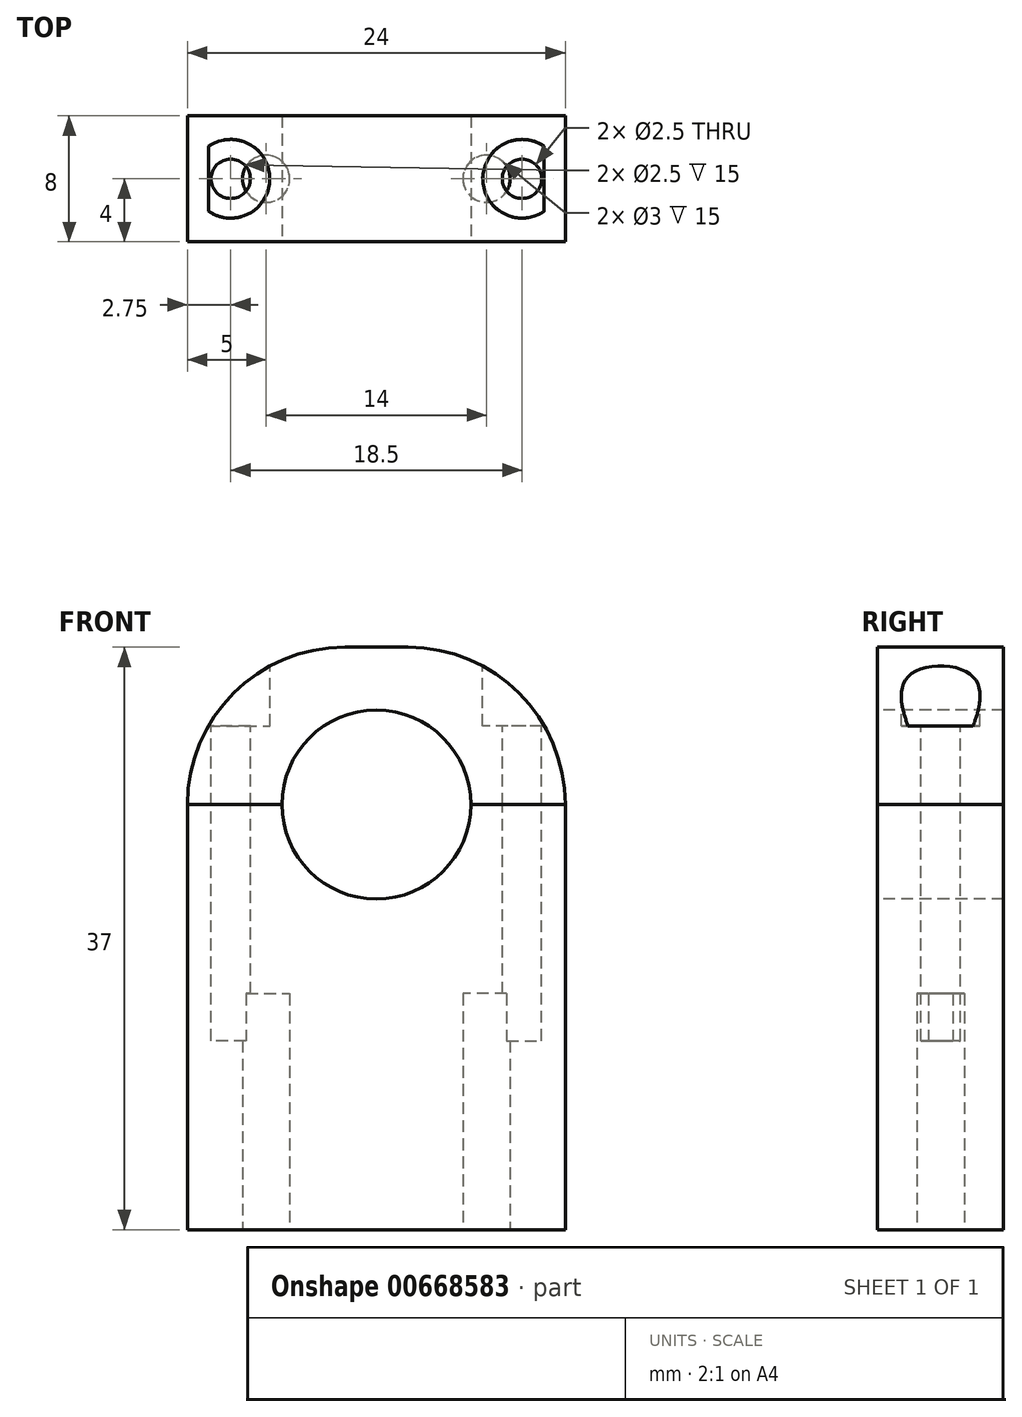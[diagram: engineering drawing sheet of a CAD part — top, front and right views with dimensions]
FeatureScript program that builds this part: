
annotation { "Feature Type Name" : "Feature", "Feature Type Description" : "" }
export const myFeature = defineFeature(function(context is Context, id is Id, definition is map)
    precondition{}
    {
        {
            var Q0;
            Q0=qCreatedBy(makeId("Top.planeOp"),FACE);
            var sketch = newSketch(context, id + "F0", { "sketchPlane" : qUnion([Q0])});
            skLineSegment(sketch, "E0.bottom", {"start": v(12, -4) * mm, "end": v(-12, -4) * mm});
            skLineSegment(sketch, "E0.top", {"start": v(12, 4) * mm, "end": v(-12, 4) * mm});
            skLineSegment(sketch, "E0.left", {"start": v(12, -4) * mm, "end": v(12, 4) * mm});
            skLineSegment(sketch, "E0.right", {"start": v(-12, -4) * mm, "end": v(-12, 4) * mm});
            skPoint(sketch, "E0.middle", {"position": v(0, 0) * mm});
            skSolve(sketch);
        }
        {
            var Q0;
            Q0 = qSketchRegion(id + "F0", true);
            extrude(context, id + "F1", {"entities" : qUnion([Q0]), "oppositeDirection" : true, "depth" : 27 * mm, "offsetDistance" : 25 * mm});
        }
        {
            var Q0;
            Q0=qCreatedBy(makeId("Top.planeOp"),FACE);
            var sketch = newSketch(context, id + "F2", { "sketchPlane" : qUnion([Q0])});
            skLineSegment(sketch, "E1.bottom", {"start": v(12, 4) * mm, "end": v(-12, 4) * mm});
            skLineSegment(sketch, "E1.top", {"start": v(12, -4) * mm, "end": v(-12, -4) * mm});
            skLineSegment(sketch, "E1.left", {"start": v(12, 4) * mm, "end": v(12, -4) * mm});
            skLineSegment(sketch, "E1.right", {"start": v(-12, 4) * mm, "end": v(-12, -4) * mm});
            skPoint(sketch, "E1.middle", {"position": v(0, 0) * mm});
            skSolve(sketch);
        }
        {
            var Q0;
            Q0 = qSketchRegion(id + "F2", true);
            extrude(context, id + "F3", {"entities" : qUnion([Q0]), "depth" : 10 * mm, "offsetDistance" : 25 * mm});
        }
        {
            var Q0;
            Q0=qCreatedBy(makeId("Front.planeOp"),FACE);
            var sketch = newSketch(context, id + "F4", { "sketchPlane" : qUnion([Q0])});
            skCircle(sketch, "E2", {"center": v(0, 0) * mm, "radius": 6 * mm});
            skSolve(sketch);
        }
        {
            var Q0;
            Q0 = qSketchRegion(id + "F4", true);
            extrude(context, id + "F5", {"entities" : qUnion([Q0]), "operationType" : NewBodyOperationType.REMOVE, "endBound" : BoundingType.SYMMETRIC, "oppositeDirection" : true, "depth" : 25 * mm, "offsetDistance" : 25 * mm});
        }
        {
            var Q0;
            Q0=makeQuery(id+"F3.opExtrude","CAP_FACE",FACE,{"disambiguationData":[OSD([sQuery(id+"F2.wireOp",EDGE,"E1.bottom"),sQuery(id+"F2.wireOp",EDGE,"E1.top"),sQuery(id+"F2.wireOp",EDGE,"E1.left"),sQuery(id+"F2.wireOp",EDGE,"E1.right")])],"isStart":false});
            var sketch = newSketch(context, id + "F6", { "sketchPlane" : qUnion([Q0])});
            skCircle(sketch, "E3", {"center": v(9.25, 0) * mm, "radius": 1.25 * mm});
            skCircle(sketch, "E4.MirrorC", {"center": v(-9.25, 0) * mm, "radius": 1.25 * mm});
            skSolve(sketch);
        }
        {
            var Q0;
            Q0 = qSketchRegion(id + "F6", true);
            extrude(context, id + "F7", {"entities" : qUnion([Q0]), "operationType" : NewBodyOperationType.REMOVE, "oppositeDirection" : true, "depth" : 25 * mm, "offsetDistance" : 25 * mm});
        }
        {
            var Q0;
            Q0=makeQuery(id+"F1.opExtrude","CAP_FACE",FACE,{"disambiguationData":[OSD([sQuery(id+"F0.wireOp",EDGE,"E0.bottom"),sQuery(id+"F0.wireOp",EDGE,"E0.top"),sQuery(id+"F0.wireOp",EDGE,"E0.left"),sQuery(id+"F0.wireOp",EDGE,"E0.right")])],"isStart":false});
            var sketch = newSketch(context, id + "F8", { "sketchPlane" : qUnion([Q0])});
            skCircle(sketch, "E5", {"center": v(7, 0) * mm, "radius": 1.5 * mm});
            skCircle(sketch, "E6.MirrorC", {"center": v(-7, 0) * mm, "radius": 1.5 * mm});
            skSolve(sketch);
        }
        {
            var Q0;
            Q0 = qSketchRegion(id + "F8", true);
            extrude(context, id + "F9", {"entities" : qUnion([Q0]), "operationType" : NewBodyOperationType.REMOVE, "oppositeDirection" : true, "depth" : 15 * mm, "offsetDistance" : 25 * mm});
        }
        {
            var Q0;
            Q0=makeQuery(id+"F3.opExtrude","CAP_FACE",FACE,{"disambiguationData":[OSD([sQuery(id+"F2.wireOp",EDGE,"E1.bottom"),sQuery(id+"F2.wireOp",EDGE,"E1.top"),sQuery(id+"F2.wireOp",EDGE,"E1.left"),sQuery(id+"F2.wireOp",EDGE,"E1.right")])],"isStart":false});
            var sketch = newSketch(context, id + "F10", { "sketchPlane" : qUnion([Q0])});
            skCircle(sketch, "E7", {"center": v(9.25, 0) * mm, "radius": 2.5 * mm});
            skCircle(sketch, "E8.MirrorC", {"center": v(-9.25, 0) * mm, "radius": 2.5 * mm});
            skSolve(sketch);
        }
        {
            var Q0;
            Q0 = qSketchRegion(id + "F10", true);
            extrude(context, id + "F11", {"entities" : qUnion([Q0]), "operationType" : NewBodyOperationType.REMOVE, "oppositeDirection" : true, "depth" : 5 * mm, "offsetDistance" : 25 * mm});
        }
        {
            var Q0;
            Q0=makeQuery(id+"F3.opExtrude","CAP_EDGE",EDGE,{"disambiguationData":[OSD([sQuery(id+"F2.wireOp",EDGE,"E1.left")])],"isStart":false});
            var Q1;
            Q1=makeQuery(id+"F3.opExtrude","CAP_EDGE",EDGE,{"disambiguationData":[OSD([sQuery(id+"F2.wireOp",EDGE,"E1.right")])],"isStart":false});
            fillet(context, id + "F12", {"entities" : qUnion([Q0, Q1]), "radius" : 10 * mm, "tangentPropagation" : true, "allowEdgeOverflow" : false});
        }
    });
